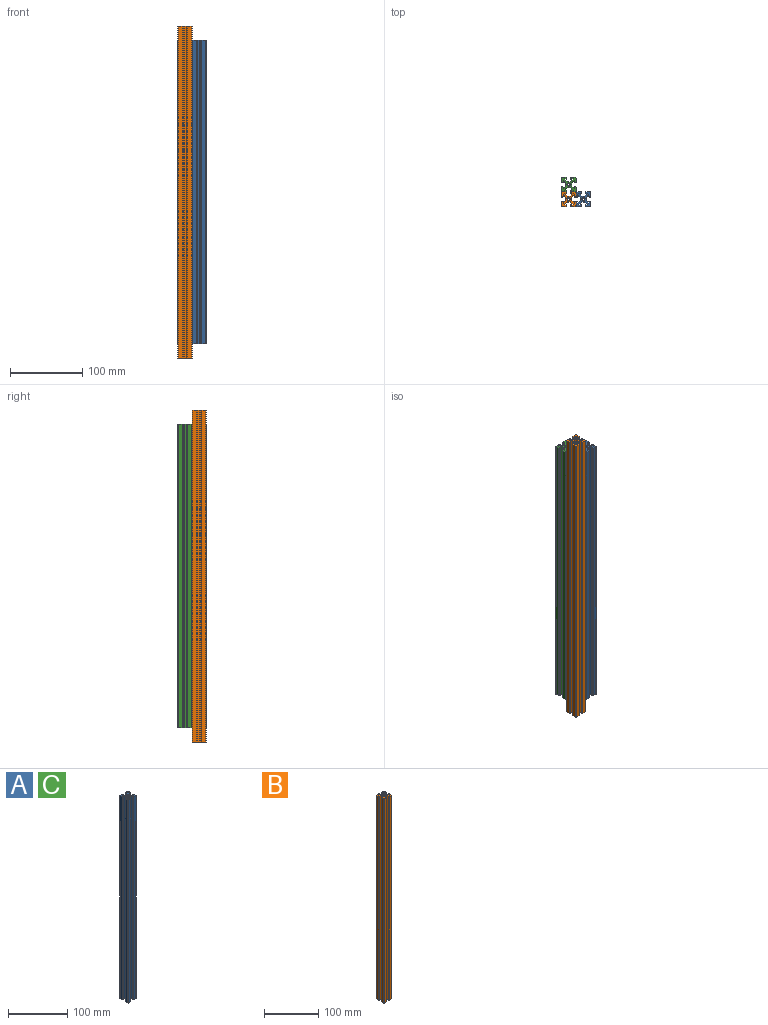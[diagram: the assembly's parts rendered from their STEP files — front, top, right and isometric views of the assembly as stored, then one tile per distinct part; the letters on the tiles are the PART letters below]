
ASSEMBLY  parts=3 mates=2
PART A: 82 faces, bbox 20x20x420 mm
  f0: cylinder r=2.1mm len=420mm, axis (0,0,-1), area 1385.6mm2, adj f15,f16,f22,f62
  f1: plane 420x0.23mm, normal (0.71,-0.71,0), area 137mm2, adj f2,f15,f16,f76
  f2: plane 420x2.08mm, normal (1,0.01,0), area 873.2mm2, adj f1,f3,f15,f16
  f3: plane 420x3.71mm, normal (0.7,-0.71,0), area 2192.1mm2, adj f2,f4,f15,f16
  f4: plane 420x0.31mm, normal (0,-1,0), area 129.1mm2, adj f3,f5,f15,f16
  f5: plane 420x2.5mm, normal (-1,0,0), area 1050mm2, adj f4,f15,f16,f17
  f6: plane 420x1mm, normal (0,-1,0), area 420mm2, adj f15,f16,f17,f18
  f7: plane 420x5.5mm, normal (1,0,0), area 2310mm2, adj f15,f16,f18,f21
  f8: plane 420x5.5mm, normal (0,1,0), area 2310mm2, adj f15,f16,f19,f21
  f9: plane 420x1mm, normal (-1,0,0), area 420mm2, adj f15,f16,f19,f20
  f10: plane 420x2.5mm, normal (0,-1,0), area 1050mm2, adj f11,f15,f16,f20
  f11: plane 420x0.31mm, normal (-1,0,0), area 129.1mm2, adj f10,f12,f15,f16
  f12: plane 420x3.71mm, normal (-0.7,0.71,0), area 2192.1mm2, adj f11,f13,f15,f16
  f13: plane 420x2.08mm, normal (-0.01,1,0), area 873.2mm2, adj f12,f14,f15,f16
  f14: plane 420x0.23mm, normal (-0.71,0.71,0), area 136.8mm2, adj f13,f15,f16,f23
  f15: plane 20x20mm, normal (0,0,1), area 198.9mm2, adj f0,f1,f2,f3,f4,f5,f6,f7
  f16: plane 20x20mm, normal (0,0,-1), area 198.8mm2, adj f0,f1,f2,f3,f4,f5,f6,f7
  f17: cylinder r=0.5mm len=420mm, axis (0,0,1), area 329.9mm2, adj f5,f6,f15,f16
  f18: cylinder r=0.5mm len=420mm, axis (0,0,-1), area 329.9mm2, adj f6,f7,f15,f16
  f19: cylinder r=0.5mm len=420mm, axis (0,0,-1), area 329.9mm2, adj f8,f9,f15,f16
  f20: cylinder r=0.5mm len=420mm, axis (0,0,-1), area 329.9mm2, adj f9,f10,f15,f16
  f21: cylinder r=1mm len=420mm, axis (0,0,-1), area 659.7mm2, adj f7,f8,f15,f16
  f22: cylinder r=2.1mm len=420mm, axis (0,0,-1), area 1385.6mm2, adj f0,f15,f16,f42
  f23: plane 420x0.23mm, normal (0.71,0.71,0), area 137mm2, adj f14,f15,f16,f24
  f24: plane 420x2.08mm, normal (-0.01,1,0), area 873.2mm2, adj f15,f16,f23,f25
  f25: plane 420x3.71mm, normal (0.71,0.7,0), area 2192.1mm2, adj f15,f16,f24,f26
  f26: plane 420x0.31mm, normal (1,0,0), area 129.1mm2, adj f15,f16,f25,f27
  f27: plane 420x2.5mm, normal (0,-1,0), area 1050mm2, adj f15,f16,f26,f37
  f28: plane 420x1mm, normal (1,0,0), area 420mm2, adj f15,f16,f37,f38
  f29: plane 420x5.5mm, normal (0,1,0), area 2310mm2, adj f15,f16,f38,f41
  f30: plane 420x5.5mm, normal (-1,0,0), area 2310mm2, adj f15,f16,f39,f41
  f31: plane 420x1mm, normal (0,-1,0), area 420mm2, adj f15,f16,f39,f40
  f32: plane 420x2.5mm, normal (1,0,0), area 1050mm2, adj f15,f16,f33,f40
  f33: plane 420x0.31mm, normal (0,-1,0), area 129.1mm2, adj f15,f16,f32,f34
  f34: plane 420x3.71mm, normal (-0.71,-0.7,0), area 2192.1mm2, adj f15,f16,f33,f35
  f35: plane 420x2.08mm, normal (-1,-0.01,0), area 873.2mm2, adj f15,f16,f34,f36
  f36: plane 420x0.23mm, normal (-0.71,-0.71,0), area 136.8mm2, adj f15,f16,f35,f43
  f37: cylinder r=0.5mm len=420mm, axis (0,0,1), area 329.9mm2, adj f15,f16,f27,f28
  f38: cylinder r=0.5mm len=420mm, axis (0,0,-1), area 329.9mm2, adj f15,f16,f28,f29
  f39: cylinder r=0.5mm len=420mm, axis (0,0,-1), area 329.9mm2, adj f15,f16,f30,f31
  f40: cylinder r=0.5mm len=420mm, axis (0,0,-1), area 329.9mm2, adj f15,f16,f31,f32
  f41: cylinder r=1mm len=420mm, axis (0,0,-1), area 659.7mm2, adj f15,f16,f29,f30
  f42: cylinder r=2.1mm len=420mm, axis (0,0,-1), area 1385.6mm2, adj f15,f16,f22,f62
  f43: plane 420x0.23mm, normal (-0.71,0.71,0), area 137mm2, adj f15,f16,f36,f44
  f44: plane 420x2.08mm, normal (-1,-0.01,0), area 873.2mm2, adj f15,f16,f43,f45
  f45: plane 420x3.71mm, normal (-0.7,0.71,0), area 2192.1mm2, adj f15,f16,f44,f46
  f46: plane 420x0.31mm, normal (0,1,0), area 129.1mm2, adj f15,f16,f45,f47
  f47: plane 420x2.5mm, normal (1,0,0), area 1050mm2, adj f15,f16,f46,f57
  f48: plane 420x1mm, normal (0,1,0), area 420mm2, adj f15,f16,f57,f58
  f49: plane 420x5.5mm, normal (-1,0,0), area 2310mm2, adj f15,f16,f58,f61
  f50: plane 420x5.5mm, normal (0,-1,0), area 2310mm2, adj f15,f16,f59,f61
  f51: plane 420x1mm, normal (1,0,0), area 420mm2, adj f15,f16,f59,f60
  f52: plane 420x2.5mm, normal (0,1,0), area 1050mm2, adj f15,f16,f53,f60
  f53: plane 420x0.31mm, normal (1,0,0), area 129.1mm2, adj f15,f16,f52,f54
  f54: plane 420x3.71mm, normal (0.7,-0.71,0), area 2192.1mm2, adj f15,f16,f53,f55
  f55: plane 420x2.08mm, normal (0.01,-1,0), area 873.2mm2, adj f15,f16,f54,f56
  f56: plane 420x0.23mm, normal (0.71,-0.71,0), area 136.8mm2, adj f15,f16,f55,f63
  f57: cylinder r=0.5mm len=420mm, axis (0,0,1), area 329.9mm2, adj f15,f16,f47,f48
  f58: cylinder r=0.5mm len=420mm, axis (0,0,-1), area 329.9mm2, adj f15,f16,f48,f49
  f59: cylinder r=0.5mm len=420mm, axis (0,0,-1), area 329.9mm2, adj f15,f16,f50,f51
  f60: cylinder r=0.5mm len=420mm, axis (0,0,-1), area 329.9mm2, adj f15,f16,f51,f52
  f61: cylinder r=1mm len=420mm, axis (0,0,-1), area 659.7mm2, adj f15,f16,f49,f50
  f62: cylinder r=2.1mm len=420mm, axis (0,0,-1), area 1385.6mm2, adj f0,f15,f16,f42
  f63: plane 420x0.23mm, normal (-0.71,-0.71,0), area 137mm2, adj f15,f16,f56,f64
  f64: plane 420x2.08mm, normal (0.01,-1,0), area 873.2mm2, adj f15,f16,f63,f65
  f65: plane 420x3.71mm, normal (-0.71,-0.7,0), area 2192.1mm2, adj f15,f16,f64,f66
  f66: plane 420x0.31mm, normal (-1,0,0), area 129.1mm2, adj f15,f16,f65,f67
  f67: plane 420x2.5mm, normal (0,1,0), area 1050mm2, adj f15,f16,f66,f77
  f68: plane 420x1mm, normal (-1,0,0), area 420mm2, adj f15,f16,f77,f78
  f69: plane 420x5.5mm, normal (0,-1,0), area 2310mm2, adj f15,f16,f78,f81
  f70: plane 420x5.5mm, normal (1,0,0), area 2310mm2, adj f15,f16,f79,f81
  f71: plane 420x1mm, normal (0,1,0), area 420mm2, adj f15,f16,f79,f80
  f72: plane 420x2.5mm, normal (-1,0,0), area 1050mm2, adj f15,f16,f73,f80
  f73: plane 420x0.31mm, normal (0,1,0), area 129.1mm2, adj f15,f16,f72,f74
  f74: plane 420x3.71mm, normal (0.71,0.7,0), area 2192.1mm2, adj f15,f16,f73,f75
  f75: plane 420x2.08mm, normal (1,0.01,0), area 873.2mm2, adj f15,f16,f74,f76
  f76: plane 420x0.23mm, normal (0.71,0.71,0), area 136.8mm2, adj f1,f15,f16,f75
  f77: cylinder r=0.5mm len=420mm, axis (0,0,1), area 329.9mm2, adj f15,f16,f67,f68
  f78: cylinder r=0.5mm len=420mm, axis (0,0,-1), area 329.9mm2, adj f15,f16,f68,f69
  f79: cylinder r=0.5mm len=420mm, axis (0,0,-1), area 329.9mm2, adj f15,f16,f70,f71
  f80: cylinder r=0.5mm len=420mm, axis (0,0,-1), area 329.9mm2, adj f15,f16,f71,f72
  f81: cylinder r=1mm len=420mm, axis (0,0,-1), area 659.7mm2, adj f15,f16,f69,f70
PART B: 82 faces, bbox 20x20x460 mm
  f0: cylinder r=2.1mm len=460mm, axis (0,0,-1), area 1517.6mm2, adj f15,f16,f22,f62
  f1: plane 460x0.23mm, normal (0.71,-0.71,0), area 150mm2, adj f2,f15,f16,f76
  f2: plane 460x2.08mm, normal (1,0.01,0), area 956.4mm2, adj f1,f3,f15,f16
  f3: plane 460x3.71mm, normal (0.7,-0.71,0), area 2400.9mm2, adj f2,f4,f15,f16
  f4: plane 460x0.31mm, normal (0,-1,0), area 141.4mm2, adj f3,f5,f15,f16
  f5: plane 460x2.5mm, normal (-1,0,0), area 1150mm2, adj f4,f15,f16,f17
  f6: plane 460x1mm, normal (0,-1,0), area 460mm2, adj f15,f16,f17,f18
  f7: plane 460x5.5mm, normal (1,0,0), area 2530mm2, adj f15,f16,f18,f21
  f8: plane 460x5.5mm, normal (0,1,0), area 2530mm2, adj f15,f16,f19,f21
  f9: plane 460x1mm, normal (-1,0,0), area 460mm2, adj f15,f16,f19,f20
  f10: plane 460x2.5mm, normal (0,-1,0), area 1150mm2, adj f11,f15,f16,f20
  f11: plane 460x0.31mm, normal (-1,0,0), area 141.4mm2, adj f10,f12,f15,f16
  f12: plane 460x3.71mm, normal (-0.7,0.71,0), area 2400.9mm2, adj f11,f13,f15,f16
  f13: plane 460x2.08mm, normal (-0.01,1,0), area 956.4mm2, adj f12,f14,f15,f16
  f14: plane 460x0.23mm, normal (-0.71,0.71,0), area 149.9mm2, adj f13,f15,f16,f23
  f15: plane 20x20mm, normal (0,0,1), area 198.9mm2, adj f0,f1,f2,f3,f4,f5,f6,f7
  f16: plane 20x20mm, normal (0,0,-1), area 198.8mm2, adj f0,f1,f2,f3,f4,f5,f6,f7
  f17: cylinder r=0.5mm len=460mm, axis (0,0,1), area 361.3mm2, adj f5,f6,f15,f16
  f18: cylinder r=0.5mm len=460mm, axis (0,0,-1), area 361.3mm2, adj f6,f7,f15,f16
  f19: cylinder r=0.5mm len=460mm, axis (0,0,-1), area 361.3mm2, adj f8,f9,f15,f16
  f20: cylinder r=0.5mm len=460mm, axis (0,0,-1), area 361.3mm2, adj f9,f10,f15,f16
  f21: cylinder r=1mm len=460mm, axis (0,0,-1), area 722.6mm2, adj f7,f8,f15,f16
  f22: cylinder r=2.1mm len=460mm, axis (0,0,-1), area 1517.6mm2, adj f0,f15,f16,f42
  f23: plane 460x0.23mm, normal (0.71,0.71,0), area 150mm2, adj f14,f15,f16,f24
  f24: plane 460x2.08mm, normal (-0.01,1,0), area 956.4mm2, adj f15,f16,f23,f25
  f25: plane 460x3.71mm, normal (0.71,0.7,0), area 2400.9mm2, adj f15,f16,f24,f26
  f26: plane 460x0.31mm, normal (1,0,0), area 141.4mm2, adj f15,f16,f25,f27
  f27: plane 460x2.5mm, normal (0,-1,0), area 1150mm2, adj f15,f16,f26,f37
  f28: plane 460x1mm, normal (1,0,0), area 460mm2, adj f15,f16,f37,f38
  f29: plane 460x5.5mm, normal (0,1,0), area 2530mm2, adj f15,f16,f38,f41
  f30: plane 460x5.5mm, normal (-1,0,0), area 2530mm2, adj f15,f16,f39,f41
  f31: plane 460x1mm, normal (0,-1,0), area 460mm2, adj f15,f16,f39,f40
  f32: plane 460x2.5mm, normal (1,0,0), area 1150mm2, adj f15,f16,f33,f40
  f33: plane 460x0.31mm, normal (0,-1,0), area 141.4mm2, adj f15,f16,f32,f34
  f34: plane 460x3.71mm, normal (-0.71,-0.7,0), area 2400.9mm2, adj f15,f16,f33,f35
  f35: plane 460x2.08mm, normal (-1,-0.01,0), area 956.4mm2, adj f15,f16,f34,f36
  f36: plane 460x0.23mm, normal (-0.71,-0.71,0), area 149.9mm2, adj f15,f16,f35,f43
  f37: cylinder r=0.5mm len=460mm, axis (0,0,1), area 361.3mm2, adj f15,f16,f27,f28
  f38: cylinder r=0.5mm len=460mm, axis (0,0,-1), area 361.3mm2, adj f15,f16,f28,f29
  f39: cylinder r=0.5mm len=460mm, axis (0,0,-1), area 361.3mm2, adj f15,f16,f30,f31
  f40: cylinder r=0.5mm len=460mm, axis (0,0,-1), area 361.3mm2, adj f15,f16,f31,f32
  f41: cylinder r=1mm len=460mm, axis (0,0,-1), area 722.6mm2, adj f15,f16,f29,f30
  f42: cylinder r=2.1mm len=460mm, axis (0,0,-1), area 1517.6mm2, adj f15,f16,f22,f62
  f43: plane 460x0.23mm, normal (-0.71,0.71,0), area 150mm2, adj f15,f16,f36,f44
  f44: plane 460x2.08mm, normal (-1,-0.01,0), area 956.4mm2, adj f15,f16,f43,f45
  f45: plane 460x3.71mm, normal (-0.7,0.71,0), area 2400.9mm2, adj f15,f16,f44,f46
  f46: plane 460x0.31mm, normal (0,1,0), area 141.4mm2, adj f15,f16,f45,f47
  f47: plane 460x2.5mm, normal (1,0,0), area 1150mm2, adj f15,f16,f46,f57
  f48: plane 460x1mm, normal (0,1,0), area 460mm2, adj f15,f16,f57,f58
  f49: plane 460x5.5mm, normal (-1,0,0), area 2530mm2, adj f15,f16,f58,f61
  f50: plane 460x5.5mm, normal (0,-1,0), area 2530mm2, adj f15,f16,f59,f61
  f51: plane 460x1mm, normal (1,0,0), area 460mm2, adj f15,f16,f59,f60
  f52: plane 460x2.5mm, normal (0,1,0), area 1150mm2, adj f15,f16,f53,f60
  f53: plane 460x0.31mm, normal (1,0,0), area 141.4mm2, adj f15,f16,f52,f54
  f54: plane 460x3.71mm, normal (0.7,-0.71,0), area 2400.9mm2, adj f15,f16,f53,f55
  f55: plane 460x2.08mm, normal (0.01,-1,0), area 956.4mm2, adj f15,f16,f54,f56
  f56: plane 460x0.23mm, normal (0.71,-0.71,0), area 149.9mm2, adj f15,f16,f55,f63
  f57: cylinder r=0.5mm len=460mm, axis (0,0,1), area 361.3mm2, adj f15,f16,f47,f48
  f58: cylinder r=0.5mm len=460mm, axis (0,0,-1), area 361.3mm2, adj f15,f16,f48,f49
  f59: cylinder r=0.5mm len=460mm, axis (0,0,-1), area 361.3mm2, adj f15,f16,f50,f51
  f60: cylinder r=0.5mm len=460mm, axis (0,0,-1), area 361.3mm2, adj f15,f16,f51,f52
  f61: cylinder r=1mm len=460mm, axis (0,0,-1), area 722.6mm2, adj f15,f16,f49,f50
  f62: cylinder r=2.1mm len=460mm, axis (0,0,-1), area 1517.6mm2, adj f0,f15,f16,f42
  f63: plane 460x0.23mm, normal (-0.71,-0.71,0), area 150mm2, adj f15,f16,f56,f64
  f64: plane 460x2.08mm, normal (0.01,-1,0), area 956.4mm2, adj f15,f16,f63,f65
  f65: plane 460x3.71mm, normal (-0.71,-0.7,0), area 2400.9mm2, adj f15,f16,f64,f66
  f66: plane 460x0.31mm, normal (-1,0,0), area 141.4mm2, adj f15,f16,f65,f67
  f67: plane 460x2.5mm, normal (0,1,0), area 1150mm2, adj f15,f16,f66,f77
  f68: plane 460x1mm, normal (-1,0,0), area 460mm2, adj f15,f16,f77,f78
  f69: plane 460x5.5mm, normal (0,-1,0), area 2530mm2, adj f15,f16,f78,f81
  f70: plane 460x5.5mm, normal (1,0,0), area 2530mm2, adj f15,f16,f79,f81
  f71: plane 460x1mm, normal (0,1,0), area 460mm2, adj f15,f16,f79,f80
  f72: plane 460x2.5mm, normal (-1,0,0), area 1150mm2, adj f15,f16,f73,f80
  f73: plane 460x0.31mm, normal (0,1,0), area 141.4mm2, adj f15,f16,f72,f74
  f74: plane 460x3.71mm, normal (0.71,0.7,0), area 2400.9mm2, adj f15,f16,f73,f75
  f75: plane 460x2.08mm, normal (1,0.01,0), area 956.4mm2, adj f15,f16,f74,f76
  f76: plane 460x0.23mm, normal (0.71,0.71,0), area 149.9mm2, adj f1,f15,f16,f75
  f77: cylinder r=0.5mm len=460mm, axis (0,0,1), area 361.3mm2, adj f15,f16,f67,f68
  f78: cylinder r=0.5mm len=460mm, axis (0,0,-1), area 361.3mm2, adj f15,f16,f68,f69
  f79: cylinder r=0.5mm len=460mm, axis (0,0,-1), area 361.3mm2, adj f15,f16,f70,f71
  f80: cylinder r=0.5mm len=460mm, axis (0,0,-1), area 361.3mm2, adj f15,f16,f71,f72
  f81: cylinder r=1mm len=460mm, axis (0,0,-1), area 722.6mm2, adj f15,f16,f69,f70
PART C: same geometry as A
PLACE A t=(20,160,126)mm
PLACE B t=(0,160,106)mm
PLACE C t=(0,180,126)mm
MATE fastened A.f49 <-> B.f70  axis (-1,0,0) through (10,153.75,336)mm
MATE fastened C.f50 <-> B.f29  axis (0,-1,0) through (-6.25,170,336)mm
